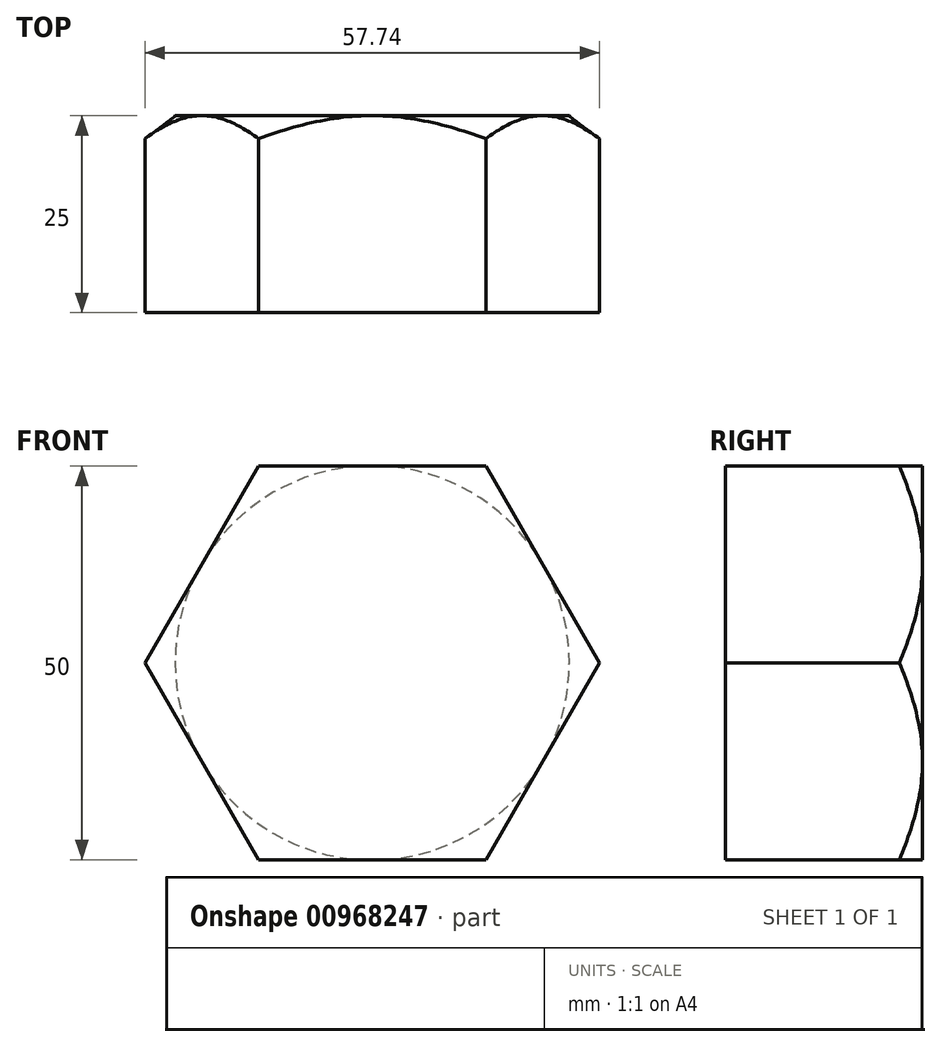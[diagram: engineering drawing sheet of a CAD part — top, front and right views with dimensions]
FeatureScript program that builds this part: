
annotation { "Feature Type Name" : "Feature", "Feature Type Description" : "" }
export const myFeature = defineFeature(function(context is Context, id is Id, definition is map)
    precondition{}
    {
        {
            var Q0;
            Q0=qCreatedBy(makeId("Front.planeOp"),FACE);
            var sketch = newSketch(context, id + "F0", { "sketchPlane" : qUnion([Q0])});
            skCircle(sketch, "E0.cCircle", {"center": v(0, 0) * mm, "radius": 25 * mm, "construction": true});
            skLineSegment(sketch, "E0.0", {"start": v(14.43, -25) * mm, "end": v(-14.43, -25) * mm});
            skLineSegment(sketch, "E0.1", {"start": v(-14.43, -25) * mm, "end": v(-28.87, 0) * mm});
            skLineSegment(sketch, "E0.2", {"start": v(-28.87, 0) * mm, "end": v(-14.43, 25) * mm});
            skLineSegment(sketch, "E0.3", {"start": v(-14.43, 25) * mm, "end": v(14.43, 25) * mm});
            skLineSegment(sketch, "E0.4", {"start": v(14.43, 25) * mm, "end": v(28.87, 0) * mm});
            skLineSegment(sketch, "E0.5", {"start": v(28.87, 0) * mm, "end": v(14.43, -25) * mm});
            skPoint(sketch, "E0.0.midPoint", {"position": v(0, -25) * mm});
            skSolve(sketch);
        }
        {
            var Q0;
            Q0=makeQuery(id+"F0.imprint","IMPRINT",FACE,{"disambiguationData":[TD([[makeQuery(id+"F0.imprint","IMPRINT",EDGE,{"derivedFrom":sQuery(id+"F0.wireOp",EDGE,"E0.0")}),-1.0]])]});
            extrude(context, id + "F1", {"entities" : qUnion([Q0]), "depth" : 25 * mm, "offsetDistance" : 25 * mm});
        }
        {
            var Q0;
            Q0=sQuery(id+"F0.wireOp",EDGE,"E0.3");
            var Q1;
            Q1=sQuery(id+"F0.wireOp",VERTEX,"E0.2.end");
            cPlane(context, id + "F2", {"entities" : qUnion([Q0, Q1]), "cplaneType" : CPlaneType.LINE_POINT, "offset" : 25 * mm, "width" : 150 * mm, "height" : 150 * mm});
        }
        {
            var Q0;
            Q0=qCreatedBy(id+"F2.planeOp",FACE);
            var sketch = newSketch(context, id + "F3", { "sketchPlane" : qUnion([Q0])});
            skPoint(sketch, "E1.0", {"position": v(0, 25) * mm});
            skLineSegment(sketch, "E2", {"start": v(-2.92, 25) * mm, "end": v(2.63, 25) * mm});
            skLineSegment(sketch, "E3", {"start": v(2.63, 25) * mm, "end": v(0, 20.45) * mm});
            skLineSegment(sketch, "E4", {"start": v(0, 20.45) * mm, "end": v(-2.92, 25) * mm});
            skSolve(sketch);
        }
        {
            var Q0;
            Q0=makeQuery(id+"F0.imprint","IMPRINT",FACE,{"disambiguationData":[TD([[makeQuery(id+"F0.imprint","IMPRINT",EDGE,{"derivedFrom":sQuery(id+"F0.wireOp",EDGE,"E0.0")}),-1.0]])]});
            var sketch = newSketch(context, id + "F4", { "sketchPlane" : qUnion([Q0])});
            skCircle(sketch, "E5.0", {"center": v(0, 0) * mm, "radius": 25 * mm});
            skSolve(sketch);
        }
        {
            var Q0;
            Q0=makeQuery(id+"F3.imprint","IMPRINT",FACE,{"disambiguationData":[TD([[makeQuery(id+"F3.imprint","IMPRINT",EDGE,{"derivedFrom":sQuery(id+"F3.wireOp",EDGE,"E2")}),-1.0]])]});
            var Q1;
            Q1=sQuery(id+"F4.wireOp",EDGE,"E5.0");
            sweep(context, id + "F5", {"operationType" : NewBodyOperationType.REMOVE, "profiles" : qUnion([Q0]), "path" : qUnion([Q1])});
        }
    });
